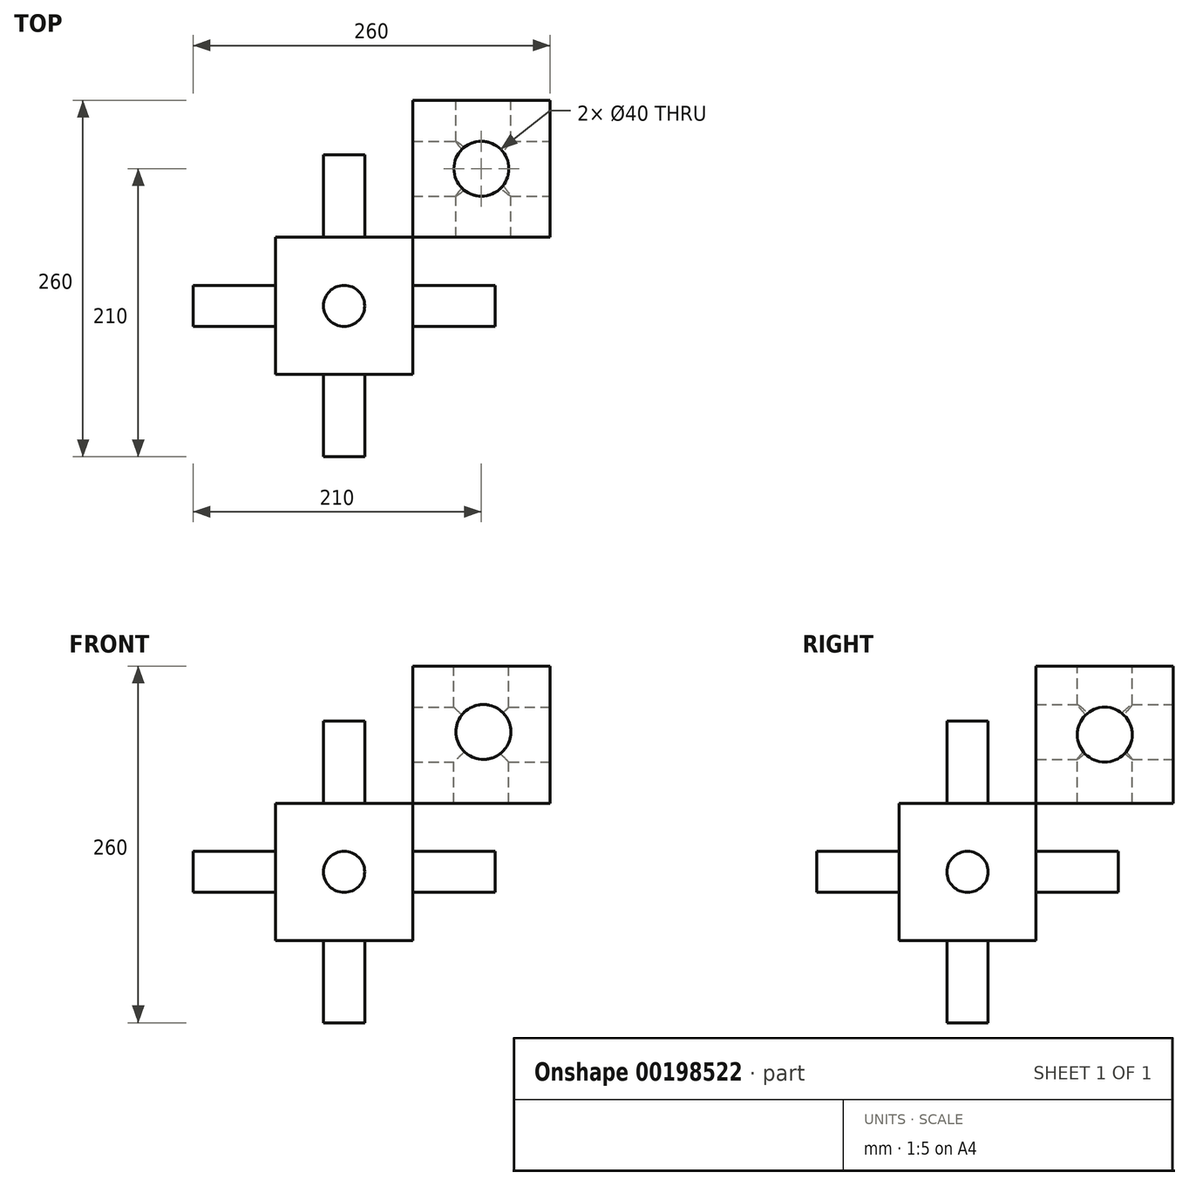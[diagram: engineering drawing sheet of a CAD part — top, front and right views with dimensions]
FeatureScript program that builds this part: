
annotation { "Feature Type Name" : "Feature", "Feature Type Description" : "" }
export const myFeature = defineFeature(function(context is Context, id is Id, definition is map)
    precondition{}
    {
        {
            var Q0;
            Q0=qCreatedBy(makeId("Top.planeOp"),FACE);
            var sketch = newSketch(context, id + "F0", { "sketchPlane" : qUnion([Q0])});
            skLineSegment(sketch, "E0", {"start": v(0, 0) * mm, "end": v(0, 100) * mm});
            skLineSegment(sketch, "E1", {"start": v(0, 100) * mm, "end": v(100, 100) * mm});
            skLineSegment(sketch, "E2", {"start": v(100, 100) * mm, "end": v(100, 0) * mm});
            skLineSegment(sketch, "E3", {"start": v(100, 0) * mm, "end": v(0, 0) * mm});
            skSolve(sketch);
        }
        {
            var Q0;
            Q0=makeQuery(id+"F0.imprint","IMPRINT",FACE,{"disambiguationData":[TD([[makeQuery(id+"F0.imprint","IMPRINT",EDGE,{"derivedFrom":sQuery(id+"F0.wireOp",EDGE,"E0")}),-1.0]])]});
            extrude(context, id + "F1", {"entities" : qUnion([Q0]), "depth" : 100 * mm});
        }
        {
            var Q0;
            Q0=makeQuery(id+"F1.opExtrude","SWEPT_FACE",FACE,{"disambiguationData":[OSD([sQuery(id+"F0.wireOp",EDGE,"E1")])]});
            var sketch = newSketch(context, id + "F2", { "sketchPlane" : qUnion([Q0])});
            skCircle(sketch, "E4", {"center": v(-51.47, 51.97) * mm, "radius": 20 * mm});
            skSolve(sketch);
        }
        {
            var Q0;
            Q0=makeQuery(id+"F2.imprint","IMPRINT",FACE,{"disambiguationData":[TD([[makeQuery(id+"F2.imprint","IMPRINT",EDGE,{"derivedFrom":sQuery(id+"F2.wireOp",EDGE,"E4")}),1.0]])]});
            extrude(context, id + "F3", {"entities" : qUnion([Q0]), "operationType" : NewBodyOperationType.REMOVE, "oppositeDirection" : true, "depth" : 132.08 * mm});
        }
        {
            var Q0;
            Q0=makeQuery(id+"F1.opExtrude","SWEPT_FACE",FACE,{"disambiguationData":[OSD([sQuery(id+"F0.wireOp",EDGE,"E2")])]});
            var sketch = newSketch(context, id + "F4", { "sketchPlane" : qUnion([Q0])});
            skCircle(sketch, "E5", {"center": v(50, 50) * mm, "radius": 20 * mm});
            skSolve(sketch);
        }
        {
            var Q0;
            Q0=makeQuery(id+"F4.imprint","IMPRINT",FACE,{"disambiguationData":[TD([[makeQuery(id+"F4.imprint","IMPRINT",EDGE,{"derivedFrom":sQuery(id+"F4.wireOp",EDGE,"E5")}),1.0]])]});
            extrude(context, id + "F5", {"entities" : qUnion([Q0]), "operationType" : NewBodyOperationType.REMOVE, "oppositeDirection" : true, "depth" : 119.13 * mm});
        }
        {
            var Q0;
            Q0=makeQuery(id+"F1.opExtrude","SWEPT_FACE",FACE,{"disambiguationData":[OSD([sQuery(id+"F0.wireOp",EDGE,"E3")])]});
            var sketch = newSketch(context, id + "F6", { "sketchPlane" : qUnion([Q0])});
            skSolve(sketch);
        }
        {
            var Q0;
            Q0=makeQuery(id+"F1.opExtrude","CAP_FACE",FACE,{"disambiguationData":[OSD([sQuery(id+"F0.wireOp",EDGE,"E0"),sQuery(id+"F0.wireOp",EDGE,"E1"),sQuery(id+"F0.wireOp",EDGE,"E2"),sQuery(id+"F0.wireOp",EDGE,"E3")])],"isStart":false});
            var sketch = newSketch(context, id + "F7", { "sketchPlane" : qUnion([Q0])});
            skCircle(sketch, "E6", {"center": v(50, 50) * mm, "radius": 20 * mm});
            skSolve(sketch);
        }
        {
            var Q0;
            Q0=makeQuery(id+"F7.imprint","IMPRINT",FACE,{"disambiguationData":[TD([[makeQuery(id+"F7.imprint","IMPRINT",EDGE,{"derivedFrom":sQuery(id+"F7.wireOp",EDGE,"E6")}),1.0]])]});
            extrude(context, id + "F8", {"entities" : qUnion([Q0]), "operationType" : NewBodyOperationType.REMOVE, "oppositeDirection" : true, "depth" : 126.24 * mm});
        }
        {
            var Q0;
            Q0=qCreatedBy(makeId("Front.planeOp"),FACE);
            var sketch = newSketch(context, id + "F9", { "sketchPlane" : qUnion([Q0])});
            skLineSegment(sketch, "E7", {"start": v(0, 0) * mm, "end": v(-100, 0) * mm});
            skLineSegment(sketch, "E8", {"start": v(-100, 0) * mm, "end": v(-100, -100) * mm});
            skLineSegment(sketch, "E9", {"start": v(-100, -100) * mm, "end": v(0, -100) * mm});
            skLineSegment(sketch, "E10", {"start": v(0, -100) * mm, "end": v(0, 0) * mm});
            skSolve(sketch);
        }
        {
            var Q0;
            Q0=makeQuery(id+"F9.imprint","IMPRINT",FACE,{"disambiguationData":[TD([[makeQuery(id+"F9.imprint","IMPRINT",EDGE,{"derivedFrom":sQuery(id+"F9.wireOp",EDGE,"E7")}),1.0]])]});
            extrude(context, id + "F10", {"entities" : qUnion([Q0]), "depth" : 100 * mm});
        }
        {
            var Q0;
            Q0=makeQuery(id+"F10.opExtrude","CAP_FACE",FACE,{"disambiguationData":[OSD([sQuery(id+"F9.wireOp",EDGE,"E7"),sQuery(id+"F9.wireOp",EDGE,"E8"),sQuery(id+"F9.wireOp",EDGE,"E9"),sQuery(id+"F9.wireOp",EDGE,"E10")])],"isStart":false});
            var sketch = newSketch(context, id + "F11", { "sketchPlane" : qUnion([Q0])});
            skCircle(sketch, "E11", {"center": v(-50, -50) * mm, "radius": 15 * mm});
            skSolve(sketch);
        }
        {
            var Q0;
            Q0=makeQuery(id+"F11.imprint","IMPRINT",FACE,{"disambiguationData":[TD([[makeQuery(id+"F11.imprint","IMPRINT",EDGE,{"derivedFrom":sQuery(id+"F11.wireOp",EDGE,"E11")}),1.0]])]});
            extrude(context, id + "F12", {"entities" : qUnion([Q0]), "operationType" : NewBodyOperationType.ADD, "depth" : 60 * mm});
        }
        {
            var Q0;
            Q0=makeQuery(id+"F10.opExtrude","SWEPT_FACE",FACE,{"disambiguationData":[OSD([sQuery(id+"F9.wireOp",EDGE,"E8")])]});
            var sketch = newSketch(context, id + "F13", { "sketchPlane" : qUnion([Q0])});
            skCircle(sketch, "E12", {"center": v(50, -50) * mm, "radius": 15 * mm});
            skSolve(sketch);
        }
        {
            var Q0;
            Q0=makeQuery(id+"F13.imprint","IMPRINT",FACE,{"disambiguationData":[TD([[makeQuery(id+"F13.imprint","IMPRINT",EDGE,{"derivedFrom":sQuery(id+"F13.wireOp",EDGE,"E12")}),1.0]])]});
            extrude(context, id + "F14", {"entities" : qUnion([Q0]), "operationType" : NewBodyOperationType.ADD, "depth" : 60 * mm});
        }
        {
            var Q0;
            Q0=makeQuery(id+"F10.opExtrude","SWEPT_FACE",FACE,{"disambiguationData":[OSD([sQuery(id+"F9.wireOp",EDGE,"E7")])]});
            var sketch = newSketch(context, id + "F15", { "sketchPlane" : qUnion([Q0])});
            skCircle(sketch, "E13", {"center": v(-50, -50) * mm, "radius": 15 * mm});
            skSolve(sketch);
        }
        {
            var Q0;
            Q0=makeQuery(id+"F15.imprint","IMPRINT",FACE,{"disambiguationData":[TD([[makeQuery(id+"F15.imprint","IMPRINT",EDGE,{"derivedFrom":sQuery(id+"F15.wireOp",EDGE,"E13")}),1.0]])]});
            extrude(context, id + "F16", {"entities" : qUnion([Q0]), "operationType" : NewBodyOperationType.ADD, "depth" : 60 * mm});
        }
        {
            var Q0;
            Q0=makeQuery(id+"F10.opExtrude","CAP_FACE",FACE,{"disambiguationData":[OSD([sQuery(id+"F9.wireOp",EDGE,"E7"),sQuery(id+"F9.wireOp",EDGE,"E8"),sQuery(id+"F9.wireOp",EDGE,"E9"),sQuery(id+"F9.wireOp",EDGE,"E10")])],"isStart":true});
            var sketch = newSketch(context, id + "F17", { "sketchPlane" : qUnion([Q0])});
            skCircle(sketch, "E14", {"center": v(50, -50) * mm, "radius": 15 * mm});
            skSolve(sketch);
        }
        {
            var Q0;
            Q0=makeQuery(id+"F17.imprint","IMPRINT",FACE,{"disambiguationData":[TD([[makeQuery(id+"F17.imprint","IMPRINT",EDGE,{"derivedFrom":sQuery(id+"F17.wireOp",EDGE,"E14")}),1.0]])]});
            extrude(context, id + "F18", {"entities" : qUnion([Q0]), "operationType" : NewBodyOperationType.ADD, "depth" : 60 * mm});
        }
        {
            var Q0;
            Q0=makeQuery(id+"F10.opExtrude","SWEPT_FACE",FACE,{"disambiguationData":[OSD([sQuery(id+"F9.wireOp",EDGE,"E10")])]});
            var sketch = newSketch(context, id + "F19", { "sketchPlane" : qUnion([Q0])});
            skCircle(sketch, "E15", {"center": v(-50, -50) * mm, "radius": 15 * mm});
            skSolve(sketch);
        }
        {
            var Q0;
            Q0=makeQuery(id+"F19.imprint","IMPRINT",FACE,{"disambiguationData":[TD([[makeQuery(id+"F19.imprint","IMPRINT",EDGE,{"derivedFrom":sQuery(id+"F19.wireOp",EDGE,"E15")}),1.0]])]});
            extrude(context, id + "F20", {"entities" : qUnion([Q0]), "operationType" : NewBodyOperationType.ADD, "depth" : 60 * mm});
        }
        {
            var Q0;
            Q0=makeQuery(id+"F10.opExtrude","SWEPT_FACE",FACE,{"disambiguationData":[OSD([sQuery(id+"F9.wireOp",EDGE,"E9")])]});
            var sketch = newSketch(context, id + "F21", { "sketchPlane" : qUnion([Q0])});
            skCircle(sketch, "E16", {"center": v(-50, 50) * mm, "radius": 15 * mm});
            skSolve(sketch);
        }
        {
            var Q0;
            Q0=makeQuery(id+"F21.imprint","IMPRINT",FACE,{"disambiguationData":[TD([[makeQuery(id+"F21.imprint","IMPRINT",EDGE,{"derivedFrom":sQuery(id+"F21.wireOp",EDGE,"E16")}),1.0]])]});
            extrude(context, id + "F22", {"entities" : qUnion([Q0]), "operationType" : NewBodyOperationType.ADD, "depth" : 60 * mm});
        }
    });
